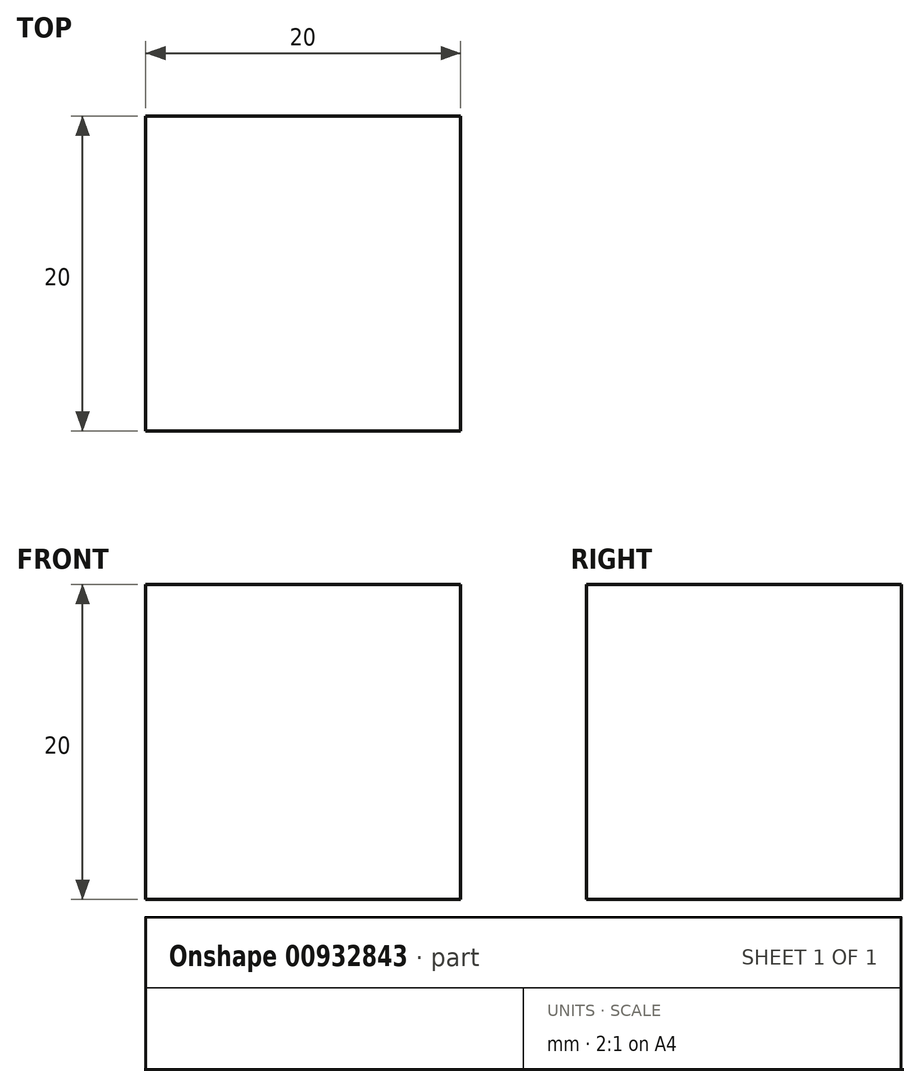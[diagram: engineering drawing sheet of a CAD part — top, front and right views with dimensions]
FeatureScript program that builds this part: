
annotation { "Feature Type Name" : "Feature", "Feature Type Description" : "" }
export const myFeature = defineFeature(function(context is Context, id is Id, definition is map)
    precondition{}
    {
        {
            var Q0;
            Q0=qCreatedBy(makeId("Front.planeOp"),FACE);
            var sketch = newSketch(context, id + "F0", { "sketchPlane" : qUnion([Q0])});
            skLineSegment(sketch, "E0.bottom", {"start": v(10, -10) * mm, "end": v(-10, -10) * mm});
            skLineSegment(sketch, "E0.top", {"start": v(10, 10) * mm, "end": v(-10, 10) * mm});
            skLineSegment(sketch, "E0.left", {"start": v(10, -10) * mm, "end": v(10, 10) * mm});
            skLineSegment(sketch, "E0.right", {"start": v(-10, -10) * mm, "end": v(-10, 10) * mm});
            skPoint(sketch, "E0.middle", {"position": v(0, 0) * mm});
            skSolve(sketch);
        }
        {
            var Q0;
            Q0 = qSketchRegion(id + "F0", true);
            extrude(context, id + "F1", {"entities" : qUnion([Q0]), "depth" : 20 * mm, "offsetDistance" : 25 * mm});
        }
    });
